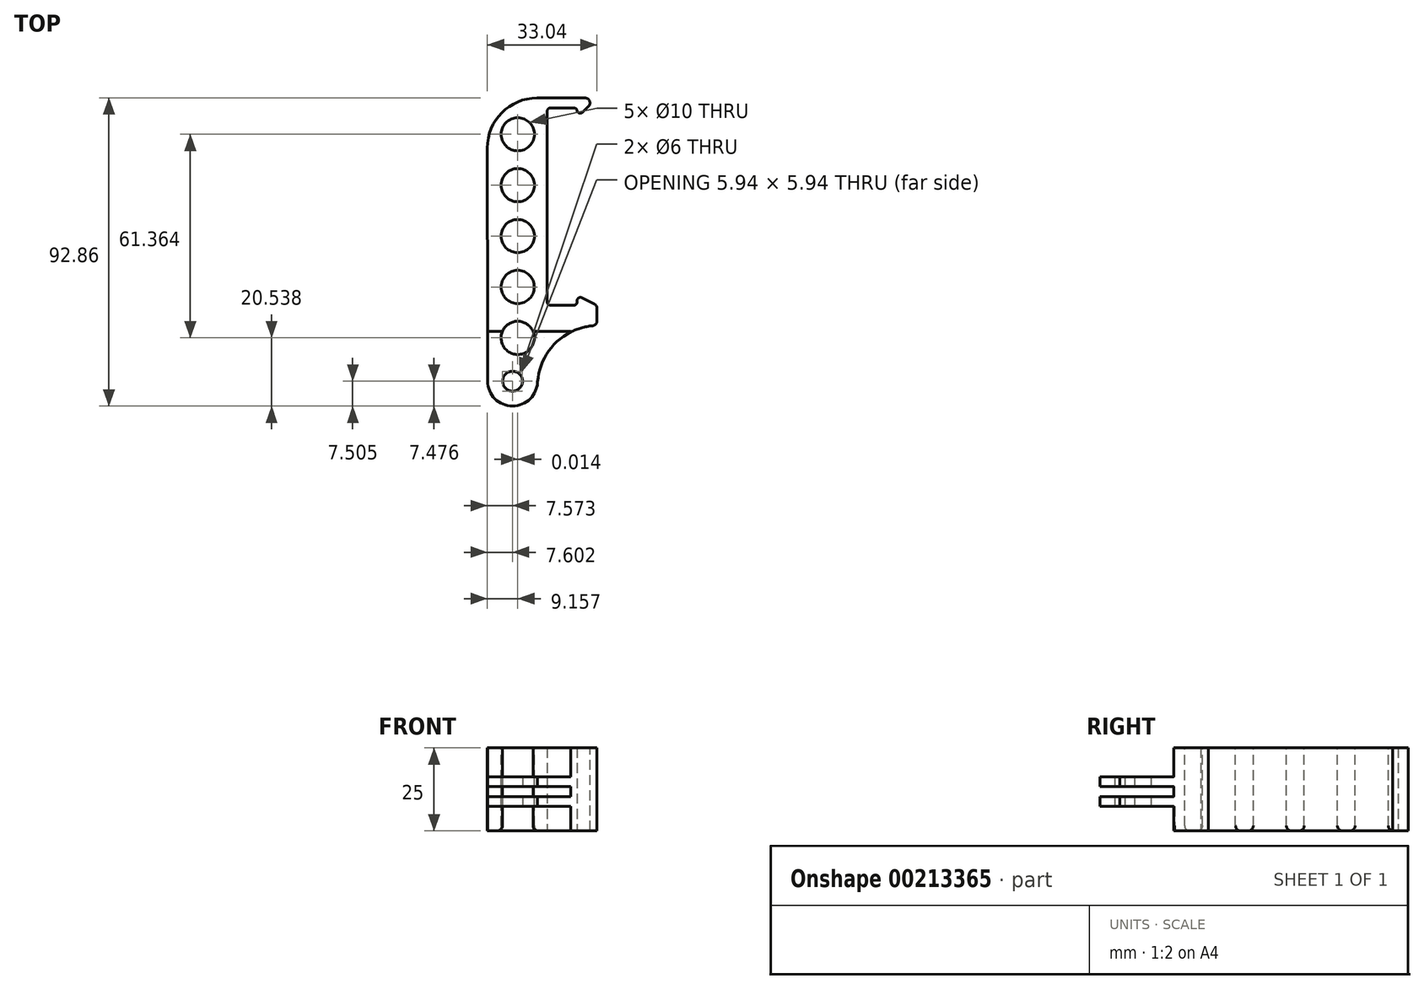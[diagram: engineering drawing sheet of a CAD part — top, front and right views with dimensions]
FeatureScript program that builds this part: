
annotation { "Feature Type Name" : "Feature", "Feature Type Description" : "" }
export const myFeature = defineFeature(function(context is Context, id is Id, definition is map)
    precondition{}
    {
        {
            var Q0;
            Q0=qCreatedBy(makeId("Top.planeOp"),FACE);
            var sketch = newSketch(context, id + "F0", { "sketchPlane" : qUnion([Q0])});
            skLineSegment(sketch, "E0.right", {"start": v(-5.96, 59.5) * mm, "end": v(-5.96, 0) * mm});
            skLineSegment(sketch, "E1.bottom", {"start": v(-5.96, 0) * mm, "end": v(3.04, 0) * mm});
            skLineSegment(sketch, "E1.right", {"start": v(9.04, 0) * mm, "end": v(9.04, -6.1) * mm});
            skLineSegment(sketch, "E2.bottom", {"start": v(-5.96, 59.5) * mm, "end": v(3.04, 59.5) * mm});
            skLineSegment(sketch, "E2.top", {"start": v(-9, 62.5) * mm, "end": v(9.04, 62.5) * mm});
            skLineSegment(sketch, "E3.left", {"start": v(3.04, 59.5) * mm, "end": v(3.04, 56.5) * mm});
            skLineSegment(sketch, "E4.left", {"start": v(3.04, 0) * mm, "end": v(3.04, 3) * mm});
            skLineSegment(sketch, "E5.left", {"start": v(-23.9, -7.86) * mm, "end": v(-23.9, -22.86) * mm});
            skLineSegment(sketch, "E5.right", {"start": v(-8.9, -22.86) * mm, "end": v(-8.9, -24.36) * mm});
            skArc(sketch, "E6", {"start": v(-23.9, -22.86) * mm, "mid": v(-16.4, -30.36) * mm, "end": v(-8.9, -22.86) * mm});
            skCircle(sketch, "E7", {"center": v(-16.4, -22.86) * mm, "radius": 3 * mm});
            skPoint(sketch, "E1.top.start.orphan", {"position": v(3.04, -3.63) * mm});
            skLineSegment(sketch, "E8", {"start": v(9.04, 0) * mm, "end": v(3.04, 3) * mm});
            skArc(sketch, "E9", {"start": v(9.04, -6.1) * mm, "mid": v(-3.66, -11.56) * mm, "end": v(-8.9, -24.36) * mm});
            skPoint(sketch, "E4.right.end.orphan", {"position": v(9.04, -0.5) * mm});
            skLineSegment(sketch, "E10", {"start": v(3.04, 56.5) * mm, "end": v(9.04, 62.5) * mm});
            skLineSegment(sketch, "E11.left", {"start": v(-23.9, -7.86) * mm, "end": v(-24, 47.4) * mm});
            skArc(sketch, "E12", {"start": v(-9, 62.5) * mm, "mid": v(-19.62, 58.04) * mm, "end": v(-24, 47.4) * mm});
            skSolve(sketch);
        }
        {
            var Q0;
            {var subQ0=sQuery(id+"F0.wireOp",EDGE,"E11.top");Q0=makeQuery(id+"F0.imprint","IMPRINT",FACE,{"disambiguationData":[TD([[makeQuery(id+"F0.imprint","IMPRINT",EDGE,{"derivedFrom":subQ0}),-1.0]])]});}
            var Q1;
            Q1=makeQuery(id+"F0.imprint","IMPRINT",FACE,{"disambiguationData":[TD([[makeQuery(id+"F0.imprint","IMPRINT",EDGE,{"derivedFrom":sQuery(id+"F0.wireOp",EDGE,"E0.right")}),-1.0]])]});
            var Q2;
            {var subQ0=sQuery(id+"F0.wireOp",EDGE,"E11.bottom");Q2=makeQuery(id+"F0.imprint","IMPRINT",FACE,{"disambiguationData":[TD([[makeQuery(id+"F0.imprint","IMPRINT",EDGE,{"derivedFrom":subQ0}),1.0]])]});}
            extrude(context, id + "F1", {"entities" : qUnion([Q0, Q1, Q2]), "depth" : 25 * mm});
        }
        {
            var Q0;
            Q0=makeQuery(id+"F1.opExtrude","SWEPT_FACE",FACE,{"disambiguationData":[OSD([sQuery(id+"F0.wireOp",EDGE,"E5.left")])]});
            var sketch = newSketch(context, id + "F2", { "sketchPlane" : qUnion([Q0])});
            skLineSegment(sketch, "E13.bottom", {"start": v(39.47, 13.32) * mm, "end": v(7.86, 13.32) * mm});
            skLineSegment(sketch, "E13.top", {"start": v(39.47, 10.32) * mm, "end": v(7.86, 10.32) * mm});
            skLineSegment(sketch, "E13.left", {"start": v(7.86, 13.32) * mm, "end": v(7.86, 10.32) * mm});
            skLineSegment(sketch, "E13.right", {"start": v(39.47, 13.32) * mm, "end": v(39.47, 10.32) * mm});
            skLineSegment(sketch, "E14.bottom", {"start": v(7.86, 13.32) * mm, "end": v(39.63, 13.32) * mm});
            skLineSegment(sketch, "E14.top", {"start": v(7.86, 16.32) * mm, "end": v(39.63, 16.32) * mm});
            skLineSegment(sketch, "E14.left", {"start": v(7.86, 13.32) * mm, "end": v(7.86, 16.32) * mm});
            skLineSegment(sketch, "E14.right", {"start": v(39.63, 13.32) * mm, "end": v(39.63, 16.32) * mm});
            skLineSegment(sketch, "E15.bottom", {"start": v(7.86, 10.32) * mm, "end": v(39.63, 10.32) * mm});
            skLineSegment(sketch, "E15.top", {"start": v(7.86, 7.32) * mm, "end": v(39.63, 7.32) * mm});
            skLineSegment(sketch, "E15.left", {"start": v(7.86, 10.32) * mm, "end": v(7.86, 7.32) * mm});
            skLineSegment(sketch, "E15.right", {"start": v(39.63, 10.32) * mm, "end": v(39.63, 7.32) * mm});
            skLineSegment(sketch, "E16.top", {"start": v(7.86, 38.98) * mm, "end": v(39.63, 38.98) * mm});
            skLineSegment(sketch, "E16.left", {"start": v(7.86, 16.32) * mm, "end": v(7.86, 38.98) * mm});
            skLineSegment(sketch, "E16.right", {"start": v(39.63, 16.32) * mm, "end": v(39.63, 38.98) * mm});
            skLineSegment(sketch, "E17.top", {"start": v(7.86, -18.68) * mm, "end": v(39.63, -18.68) * mm});
            skLineSegment(sketch, "E17.left", {"start": v(7.86, 7.32) * mm, "end": v(7.86, -18.68) * mm});
            skLineSegment(sketch, "E17.right", {"start": v(39.63, 7.32) * mm, "end": v(39.63, -18.68) * mm});
            skSolve(sketch);
        }
        {
            var Q0;
            {var subQ1=sQuery(id+"F0.wireOp",EDGE,"E5.left");var subQ6=makeQuery(id+"F1.opExtrude","CAP_EDGE",EDGE,{"disambiguationData":[OSD([subQ1])],"isStart":true});Q0=makeQuery(id+"F2.imprint","IMPRINT",FACE,{"disambiguationData":[TD([[makeQuery(id+"F2.imprint","IMPRINT",EDGE,{"derivedFrom":subQ6}),1.0]])]});}
            var Q1;
            {var subQ1=sQuery(id+"F0.wireOp",EDGE,"E5.left");var subQ6=makeQuery(id+"F1.opExtrude","CAP_EDGE",EDGE,{"disambiguationData":[OSD([subQ1])],"isStart":false});Q1=makeQuery(id+"F2.imprint","IMPRINT",FACE,{"disambiguationData":[TD([[makeQuery(id+"F2.imprint","IMPRINT",EDGE,{"derivedFrom":subQ6}),-1.0]])]});}
            var Q2;
            {var subQ1=sQuery(id+"F2.wireOp",EDGE,"E17.top");Q2=makeQuery(id+"F2.imprint","IMPRINT",FACE,{"disambiguationData":[TD([[makeQuery(id+"F2.imprint","IMPRINT",EDGE,{"derivedFrom":subQ1}),1.0]])]});}
            var Q3;
            {var subQ4=sQuery(id+"F2.wireOp",EDGE,"E16.top");Q3=makeQuery(id+"F2.imprint","IMPRINT",FACE,{"disambiguationData":[TD([[makeQuery(id+"F2.imprint","IMPRINT",EDGE,{"derivedFrom":subQ4}),-1.0]])]});}
            var Q4;
            {var subQ0=sQuery(id+"F2.wireOp",EDGE,"E13.right");Q4=makeQuery(id+"F2.imprint","IMPRINT",FACE,{"disambiguationData":[TD([[makeQuery(id+"F2.imprint","IMPRINT",EDGE,{"derivedFrom":subQ0}),-1.0]])]});}
            var Q5;
            {var subQ0=sQuery(id+"F2.wireOp",EDGE,"E13.left");Q5=makeQuery(id+"F2.imprint","IMPRINT",FACE,{"disambiguationData":[TD([[makeQuery(id+"F2.imprint","IMPRINT",EDGE,{"derivedFrom":subQ0}),1.0]])]});}
            extrude(context, id + "F3", {"entities" : qUnion([Q0, Q1, Q2, Q3, Q4, Q5]), "operationType" : NewBodyOperationType.REMOVE, "oppositeDirection" : true, "depth" : 25 * mm});
        }
        {
            var Q0;
            Q0=makeQuery(id+"F1.opExtrude","SWEPT_EDGE",EDGE,{"disambiguationData":[OSD([sQuery(id+"F0.wireOp",EDGE,"E1.right"),sQuery(id+"F0.wireOp",EDGE,"E8")])]});
            var Q1;
            Q1=makeQuery(id+"F1.opExtrude","SWEPT_EDGE",EDGE,{"disambiguationData":[OSD([sQuery(id+"F0.wireOp",EDGE,"E1.right"),sQuery(id+"F0.wireOp",EDGE,"E9")])]});
            var Q2;
            Q2=makeQuery(id+"F1.opExtrude","SWEPT_EDGE",EDGE,{"disambiguationData":[OSD([sQuery(id+"F0.wireOp",EDGE,"E2.top"),sQuery(id+"F0.wireOp",EDGE,"E10")])]});
            fillet(context, id + "F4", {"entities" : qUnion([Q0, Q1, Q2]), "radius" : 1.5 * mm, "tangentPropagation" : true, "allowEdgeOverflow" : false});
        }
        {
            var Q0;
            Q0=makeQuery(id+"F1.opExtrude","SWEPT_EDGE",EDGE,{"disambiguationData":[OSD([sQuery(id+"F0.wireOp",EDGE,"E0.right"),sQuery(id+"F0.wireOp",EDGE,"E2.bottom")])]});
            var Q1;
            Q1=makeQuery(id+"F1.opExtrude","SWEPT_EDGE",EDGE,{"disambiguationData":[OSD([sQuery(id+"F0.wireOp",EDGE,"E0.right"),sQuery(id+"F0.wireOp",EDGE,"E1.bottom")])]});
            var Q2;
            Q2=makeQuery(id+"F1.opExtrude","SWEPT_EDGE",EDGE,{"disambiguationData":[OSD([sQuery(id+"F0.wireOp",EDGE,"E2.bottom"),sQuery(id+"F0.wireOp",EDGE,"E3.left")])]});
            var Q3;
            Q3=makeQuery(id+"F1.opExtrude","SWEPT_EDGE",EDGE,{"disambiguationData":[OSD([sQuery(id+"F0.wireOp",EDGE,"E1.bottom"),sQuery(id+"F0.wireOp",EDGE,"E4.left")])]});
            fillet(context, id + "F5", {"entities" : qUnion([Q0, Q1, Q2, Q3]), "radius" : 1 * mm, "tangentPropagation" : true, "allowEdgeOverflow" : false});
        }
        {
            var Q0;
            Q0=makeQuery(id+"F1.opExtrude","CAP_FACE",FACE,{"disambiguationData":[OSD([sQuery(id+"F0.wireOp",EDGE,"E0.right"),sQuery(id+"F0.wireOp",EDGE,"E1.bottom"),sQuery(id+"F0.wireOp",EDGE,"E1.right"),sQuery(id+"F0.wireOp",EDGE,"E2.bottom"),sQuery(id+"F0.wireOp",EDGE,"E2.top"),sQuery(id+"F0.wireOp",EDGE,"E2.right"),sQuery(id+"F0.wireOp",EDGE,"E3.top"),sQuery(id+"F0.wireOp",EDGE,"E3.left"),sQuery(id+"F0.wireOp",EDGE,"E4.top"),sQuery(id+"F0.wireOp",EDGE,"E4.left"),sQuery(id+"F0.wireOp",EDGE,"E5.left"),sQuery(id+"F0.wireOp",EDGE,"E5.right"),sQuery(id+"F0.wireOp",EDGE,"E6"),sQuery(id+"F0.wireOp",EDGE,"E7"),sQuery(id+"F0.wireOp",EDGE,"vfLY6uG4-y0tV-8spB-1rVG-UtVCXCo2wCze"),sQuery(id+"F0.wireOp",EDGE,"IZeYfrJS-7V4p-GKvK-Bs6F-KUIEGbjNp2gk"),sQuery(id+"F0.wireOp",EDGE,"UbSuR1B7-Qmw8-mbvo-CxSJ-8DXWhNlOWwhV"),sQuery(id+"F0.wireOp",EDGE,"E8"),sQuery(id+"F0.wireOp",EDGE,"E9"),sQuery(id+"F0.wireOp",EDGE,"E10"),sQuery(id+"F0.wireOp",EDGE,"E11.top"),sQuery(id+"F0.wireOp",EDGE,"E11.left")])],"isStart":false});
            var sketch = newSketch(context, id + "F6", { "sketchPlane" : qUnion([Q0])});
            skLineSegment(sketch, "E18", {"start": v(23.8, 29.75) * mm, "end": v(-35.74, 29.75) * mm, "construction": true});
            skLineSegment(sketch, "E19", {"start": v(-14.86, 69.17) * mm, "end": v(-14.66, -43.1) * mm, "construction": true});
            skCircle(sketch, "E20", {"center": v(-14.83, 51.54) * mm, "radius": 5 * mm});
            skCircle(sketch, "E21.0.1.0", {"center": v(-14.83, 36.2) * mm, "radius": 5 * mm});
            skCircle(sketch, "E21.0.2.0", {"center": v(-14.84, 20.86) * mm, "radius": 5 * mm});
            skCircle(sketch, "E21.0.3.0", {"center": v(-14.84, 5.52) * mm, "radius": 5 * mm});
            skCircle(sketch, "E21.0.4.0", {"center": v(-14.84, -9.82) * mm, "radius": 5 * mm});
            skLineSegment(sketch, "E21.direction1", {"start": v(-14.83, 51.54) * mm, "end": v(10.9, 51.54) * mm, "construction": true});
            skLineSegment(sketch, "E21.direction2", {"start": v(-14.83, 51.54) * mm, "end": v(-14.83, 36.2) * mm, "construction": true});
            skSolve(sketch);
        }
        {
            var Q0;
            Q0=makeQuery(id+"F6.imprint","IMPRINT",FACE,{"disambiguationData":[TD([[makeQuery(id+"F6.imprint","IMPRINT",EDGE,{"derivedFrom":sQuery(id+"F6.wireOp",EDGE,"E20")}),1.0]])]});
            var Q1;
            Q1=makeQuery(id+"F6.imprint","IMPRINT",FACE,{"disambiguationData":[TD([[makeQuery(id+"F6.imprint","IMPRINT",EDGE,{"derivedFrom":sQuery(id+"F6.wireOp",EDGE,"E21.0.1.0")}),1.0]])]});
            var Q2;
            Q2=makeQuery(id+"F6.imprint","IMPRINT",FACE,{"disambiguationData":[TD([[makeQuery(id+"F6.imprint","IMPRINT",EDGE,{"derivedFrom":sQuery(id+"F6.wireOp",EDGE,"E21.0.3.0")}),1.0]])]});
            var Q3;
            Q3=makeQuery(id+"F6.imprint","IMPRINT",FACE,{"disambiguationData":[TD([[makeQuery(id+"F6.imprint","IMPRINT",EDGE,{"derivedFrom":sQuery(id+"F6.wireOp",EDGE,"E21.0.4.0")}),1.0]])]});
            var Q4;
            Q4=makeQuery(id+"F6.imprint","IMPRINT",FACE,{"disambiguationData":[TD([[makeQuery(id+"F6.imprint","IMPRINT",EDGE,{"derivedFrom":sQuery(id+"F6.wireOp",EDGE,"E21.0.2.0")}),1.0]])]});
            extrude(context, id + "F7", {"entities" : qUnion([Q0, Q1, Q2, Q3, Q4]), "operationType" : NewBodyOperationType.REMOVE, "oppositeDirection" : true, "depth" : 25 * mm});
        }
        {
            var Q0;
            Q0=makeQuery(id+"F1.opExtrude","SWEPT_EDGE",EDGE,{"disambiguationData":[OSD([sQuery(id+"F0.wireOp",EDGE,"E3.left"),sQuery(id+"F0.wireOp",EDGE,"E10")])]});
            var Q1;
            Q1=makeQuery(id+"F1.opExtrude","SWEPT_EDGE",EDGE,{"disambiguationData":[OSD([sQuery(id+"F0.wireOp",EDGE,"E4.left"),sQuery(id+"F0.wireOp",EDGE,"E8")])]});
            fillet(context, id + "F8", {"entities" : qUnion([Q0, Q1]), "radius" : 1 * mm, "tangentPropagation" : true, "allowEdgeOverflow" : false});
        }
        {
            var Q0;
            Q0=makeQuery(id+"F7.boolean.opBoolean","COPY",EDGE,{"derivedFrom":makeQuery(id+"F7.opExtrude","CAP_EDGE",EDGE,{"disambiguationData":[OSD([sQuery(id+"F6.wireOp",EDGE,"E20")])],"isStart":true})});
            var Q1;
            Q1=makeQuery(id+"F7.boolean.opBoolean","COPY",EDGE,{"derivedFrom":makeQuery(id+"F7.opExtrude","CAP_EDGE",EDGE,{"disambiguationData":[OSD([sQuery(id+"F6.wireOp",EDGE,"E21.0.1.0")])],"isStart":true})});
            var Q2;
            Q2=makeQuery(id+"F7.boolean.opBoolean","COPY",EDGE,{"derivedFrom":makeQuery(id+"F7.opExtrude","CAP_EDGE",EDGE,{"disambiguationData":[OSD([sQuery(id+"F6.wireOp",EDGE,"E21.0.2.0")])],"isStart":true})});
            var Q3;
            Q3=makeQuery(id+"F7.boolean.opBoolean","COPY",EDGE,{"derivedFrom":makeQuery(id+"F7.opExtrude","CAP_EDGE",EDGE,{"disambiguationData":[OSD([sQuery(id+"F6.wireOp",EDGE,"E21.0.3.0")])],"isStart":true})});
            var Q4;
            Q4=makeQuery(id+"F7.boolean.opBoolean","COPY",EDGE,{"derivedFrom":makeQuery(id+"F7.opExtrude","CAP_EDGE",EDGE,{"disambiguationData":[OSD([sQuery(id+"F6.wireOp",EDGE,"E21.0.4.0")])],"isStart":true})});
            var Q5;
            Q5=makeQuery(id+"F7.boolean.opBoolean","INTERSECT",EDGE,{"derivedFrom":[makeQuery(id+"F1.opExtrude","CAP_FACE",FACE,{"disambiguationData":[OSD([sQuery(id+"F0.wireOp",EDGE,"E0.right"),sQuery(id+"F0.wireOp",EDGE,"E1.bottom"),sQuery(id+"F0.wireOp",EDGE,"E1.right"),sQuery(id+"F0.wireOp",EDGE,"E2.bottom"),sQuery(id+"F0.wireOp",EDGE,"E2.top"),sQuery(id+"F0.wireOp",EDGE,"E3.left"),sQuery(id+"F0.wireOp",EDGE,"E4.left"),sQuery(id+"F0.wireOp",EDGE,"E5.left"),sQuery(id+"F0.wireOp",EDGE,"E6"),sQuery(id+"F0.wireOp",EDGE,"E7"),sQuery(id+"F0.wireOp",EDGE,"E8"),sQuery(id+"F0.wireOp",EDGE,"E9"),sQuery(id+"F0.wireOp",EDGE,"E10"),sQuery(id+"F0.wireOp",EDGE,"E11.left"),sQuery(id+"F0.wireOp",EDGE,"E12")])],"isStart":true}),makeQuery(id+"F7.opExtrude","SWEPT_FACE",FACE,{"disambiguationData":[OSD([sQuery(id+"F6.wireOp",EDGE,"E20")])]})]});
            var Q6;
            Q6=makeQuery(id+"F7.boolean.opBoolean","INTERSECT",EDGE,{"derivedFrom":[makeQuery(id+"F1.opExtrude","CAP_FACE",FACE,{"disambiguationData":[OSD([sQuery(id+"F0.wireOp",EDGE,"E0.right"),sQuery(id+"F0.wireOp",EDGE,"E1.bottom"),sQuery(id+"F0.wireOp",EDGE,"E1.right"),sQuery(id+"F0.wireOp",EDGE,"E2.bottom"),sQuery(id+"F0.wireOp",EDGE,"E2.top"),sQuery(id+"F0.wireOp",EDGE,"E3.left"),sQuery(id+"F0.wireOp",EDGE,"E4.left"),sQuery(id+"F0.wireOp",EDGE,"E5.left"),sQuery(id+"F0.wireOp",EDGE,"E6"),sQuery(id+"F0.wireOp",EDGE,"E7"),sQuery(id+"F0.wireOp",EDGE,"E8"),sQuery(id+"F0.wireOp",EDGE,"E9"),sQuery(id+"F0.wireOp",EDGE,"E10"),sQuery(id+"F0.wireOp",EDGE,"E11.left"),sQuery(id+"F0.wireOp",EDGE,"E12")])],"isStart":true}),makeQuery(id+"F7.opExtrude","SWEPT_FACE",FACE,{"disambiguationData":[OSD([sQuery(id+"F6.wireOp",EDGE,"E21.0.1.0")])]})]});
            var Q7;
            Q7=makeQuery(id+"F7.boolean.opBoolean","INTERSECT",EDGE,{"derivedFrom":[makeQuery(id+"F1.opExtrude","CAP_FACE",FACE,{"disambiguationData":[OSD([sQuery(id+"F0.wireOp",EDGE,"E0.right"),sQuery(id+"F0.wireOp",EDGE,"E1.bottom"),sQuery(id+"F0.wireOp",EDGE,"E1.right"),sQuery(id+"F0.wireOp",EDGE,"E2.bottom"),sQuery(id+"F0.wireOp",EDGE,"E2.top"),sQuery(id+"F0.wireOp",EDGE,"E3.left"),sQuery(id+"F0.wireOp",EDGE,"E4.left"),sQuery(id+"F0.wireOp",EDGE,"E5.left"),sQuery(id+"F0.wireOp",EDGE,"E6"),sQuery(id+"F0.wireOp",EDGE,"E7"),sQuery(id+"F0.wireOp",EDGE,"E8"),sQuery(id+"F0.wireOp",EDGE,"E9"),sQuery(id+"F0.wireOp",EDGE,"E10"),sQuery(id+"F0.wireOp",EDGE,"E11.left"),sQuery(id+"F0.wireOp",EDGE,"E12")])],"isStart":true}),makeQuery(id+"F7.opExtrude","SWEPT_FACE",FACE,{"disambiguationData":[OSD([sQuery(id+"F6.wireOp",EDGE,"E21.0.2.0")])]})]});
            var Q8;
            Q8=makeQuery(id+"F7.boolean.opBoolean","INTERSECT",EDGE,{"derivedFrom":[makeQuery(id+"F1.opExtrude","CAP_FACE",FACE,{"disambiguationData":[OSD([sQuery(id+"F0.wireOp",EDGE,"E0.right"),sQuery(id+"F0.wireOp",EDGE,"E1.bottom"),sQuery(id+"F0.wireOp",EDGE,"E1.right"),sQuery(id+"F0.wireOp",EDGE,"E2.bottom"),sQuery(id+"F0.wireOp",EDGE,"E2.top"),sQuery(id+"F0.wireOp",EDGE,"E3.left"),sQuery(id+"F0.wireOp",EDGE,"E4.left"),sQuery(id+"F0.wireOp",EDGE,"E5.left"),sQuery(id+"F0.wireOp",EDGE,"E6"),sQuery(id+"F0.wireOp",EDGE,"E7"),sQuery(id+"F0.wireOp",EDGE,"E8"),sQuery(id+"F0.wireOp",EDGE,"E9"),sQuery(id+"F0.wireOp",EDGE,"E10"),sQuery(id+"F0.wireOp",EDGE,"E11.left"),sQuery(id+"F0.wireOp",EDGE,"E12")])],"isStart":true}),makeQuery(id+"F7.opExtrude","SWEPT_FACE",FACE,{"disambiguationData":[OSD([sQuery(id+"F6.wireOp",EDGE,"E21.0.3.0")])]})]});
            var Q9;
            Q9=makeQuery(id+"F7.boolean.opBoolean","INTERSECT",EDGE,{"derivedFrom":[makeQuery(id+"F1.opExtrude","CAP_FACE",FACE,{"disambiguationData":[OSD([sQuery(id+"F0.wireOp",EDGE,"E0.right"),sQuery(id+"F0.wireOp",EDGE,"E1.bottom"),sQuery(id+"F0.wireOp",EDGE,"E1.right"),sQuery(id+"F0.wireOp",EDGE,"E2.bottom"),sQuery(id+"F0.wireOp",EDGE,"E2.top"),sQuery(id+"F0.wireOp",EDGE,"E3.left"),sQuery(id+"F0.wireOp",EDGE,"E4.left"),sQuery(id+"F0.wireOp",EDGE,"E5.left"),sQuery(id+"F0.wireOp",EDGE,"E6"),sQuery(id+"F0.wireOp",EDGE,"E7"),sQuery(id+"F0.wireOp",EDGE,"E8"),sQuery(id+"F0.wireOp",EDGE,"E9"),sQuery(id+"F0.wireOp",EDGE,"E10"),sQuery(id+"F0.wireOp",EDGE,"E11.left"),sQuery(id+"F0.wireOp",EDGE,"E12")])],"isStart":true}),makeQuery(id+"F7.opExtrude","SWEPT_FACE",FACE,{"disambiguationData":[OSD([sQuery(id+"F6.wireOp",EDGE,"E21.0.4.0")])]})]});
            fillet(context, id + "F9", {"entities" : qUnion([Q0, Q1, Q2, Q3, Q4, Q5, Q6, Q7, Q8, Q9]), "radius" : 1.5 * mm, "tangentPropagation" : true, "allowEdgeOverflow" : false});
        }
    });
